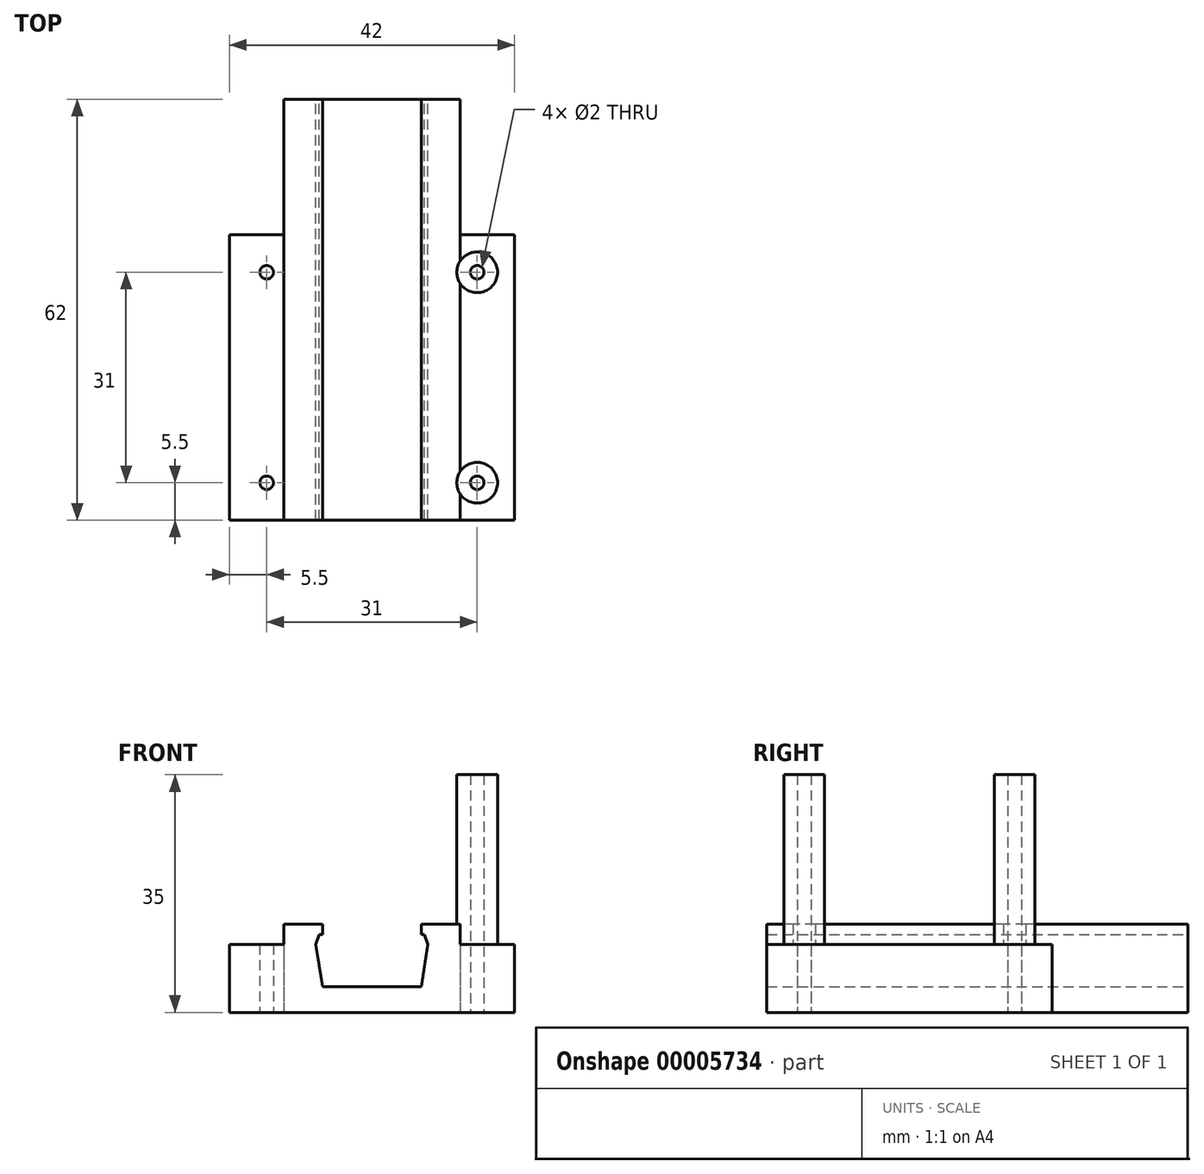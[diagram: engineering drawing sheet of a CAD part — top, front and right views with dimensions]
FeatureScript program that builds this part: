
annotation { "Feature Type Name" : "Feature", "Feature Type Description" : "" }
export const myFeature = defineFeature(function(context is Context, id is Id, definition is map)
    precondition{}
    {
        {
            var Q0;
            Q0=qCreatedBy(makeId("Top.planeOp"),FACE);
            var sketch = newSketch(context, id + "F0", { "sketchPlane" : qUnion([Q0])});
            skLineSegment(sketch, "E0.bottom", {"start": v(13, 0) * mm, "end": v(21, 0) * mm});
            skLineSegment(sketch, "E0.top", {"start": v(0, -42) * mm, "end": v(21, -42) * mm});
            skLineSegment(sketch, "E0.left", {"start": v(0, 0) * mm, "end": v(0, -42) * mm});
            skLineSegment(sketch, "E0.right", {"start": v(21, 0) * mm, "end": v(21, -42) * mm});
            skLineSegment(sketch, "E1.top", {"start": v(0, 20) * mm, "end": v(13, 20) * mm});
            skLineSegment(sketch, "E1.left", {"start": v(0, 0) * mm, "end": v(0, 20) * mm});
            skLineSegment(sketch, "E1.right", {"start": v(13, 0) * mm, "end": v(13, 20) * mm});
            skCircle(sketch, "E2", {"center": v(15.5, -5.5) * mm, "radius": 1 * mm});
            skCircle(sketch, "E3", {"center": v(15.5, -36.5) * mm, "radius": 1 * mm});
            skCircle(sketch, "E4.1.MirrorC", {"center": v(-15.5, -36.5) * mm, "radius": 1 * mm});
            skLineSegment(sketch, "E4.2.MirrorCS", {"start": v(-13, 0) * mm, "end": v(-13, 20) * mm});
            skCircle(sketch, "E4.3.MirrorC", {"center": v(-15.5, -5.5) * mm, "radius": 1 * mm});
            skLineSegment(sketch, "E4.4.MirrorCS", {"start": v(0, 20) * mm, "end": v(-13, 20) * mm});
            skLineSegment(sketch, "E4.6.MirrorCS", {"start": v(-13, 0) * mm, "end": v(-21, 0) * mm});
            skLineSegment(sketch, "E4.7.MirrorCS", {"start": v(0, -42) * mm, "end": v(-21, -42) * mm});
            skLineSegment(sketch, "E4.8.MirrorCS", {"start": v(-21, 0) * mm, "end": v(-21, -42) * mm});
            skSolve(sketch);
        }
        {
            var Q0;
            Q0=makeQuery(id+"F0.imprint","IMPRINT",FACE,{"disambiguationData":[TD([[makeQuery(id+"F0.imprint","IMPRINT",EDGE,{"derivedFrom":sQuery(id+"F0.wireOp",EDGE,"E1.left")}),1.0]])]});
            var Q1;
            Q1=makeQuery(id+"F0.imprint","IMPRINT",FACE,{"disambiguationData":[TD([[makeQuery(id+"F0.imprint","IMPRINT",EDGE,{"derivedFrom":sQuery(id+"F0.wireOp",EDGE,"E0.bottom")}),-1.0]])]});
            extrude(context, id + "F1", {"entities" : qUnion([Q0, Q1]), "depth" : 10 * mm});
        }
        {
            var Q0;
            Q0=makeQuery(id+"F1.opExtrude","CAP_FACE",FACE,{"disambiguationData":[OSD([sQuery(id+"F0.wireOp",EDGE,"E0.bottom"),sQuery(id+"F0.wireOp",EDGE,"E0.top"),sQuery(id+"F0.wireOp",EDGE,"E0.right"),sQuery(id+"F0.wireOp",EDGE,"E1.top"),sQuery(id+"F0.wireOp",EDGE,"E1.right"),sQuery(id+"F0.wireOp",EDGE,"E2"),sQuery(id+"F0.wireOp",EDGE,"E3"),sQuery(id+"F0.wireOp",EDGE,"E4.1.MirrorC"),sQuery(id+"F0.wireOp",EDGE,"E4.2.MirrorCS"),sQuery(id+"F0.wireOp",EDGE,"E4.3.MirrorC"),sQuery(id+"F0.wireOp",EDGE,"E4.4.MirrorCS"),sQuery(id+"F0.wireOp",EDGE,"E4.6.MirrorCS"),sQuery(id+"F0.wireOp",EDGE,"E4.7.MirrorCS"),sQuery(id+"F0.wireOp",EDGE,"E4.8.MirrorCS")])],"isStart":false});
            var sketch = newSketch(context, id + "F2", { "sketchPlane" : qUnion([Q0])});
            skLineSegment(sketch, "E5.bottom", {"start": v(-13, 20) * mm, "end": v(13, 20) * mm});
            skLineSegment(sketch, "E5.top", {"start": v(-13, -42) * mm, "end": v(13, -42) * mm});
            skLineSegment(sketch, "E5.left", {"start": v(-13, 20) * mm, "end": v(-13, -42) * mm});
            skLineSegment(sketch, "E5.right", {"start": v(13, 20) * mm, "end": v(13, -42) * mm});
            skLineSegment(sketch, "E6", {"start": v(0, 20) * mm, "end": v(0, 9.7) * mm});
            skLineSegment(sketch, "E7.bottom", {"start": v(-7.25, 20) * mm, "end": v(7.25, 20) * mm});
            skLineSegment(sketch, "E7.top", {"start": v(-7.25, -42) * mm, "end": v(7.25, -42) * mm});
            skLineSegment(sketch, "E7.left", {"start": v(-7.25, 20) * mm, "end": v(-7.25, -42) * mm});
            skLineSegment(sketch, "E7.right", {"start": v(7.25, 20) * mm, "end": v(7.25, -42) * mm});
            skSolve(sketch);
        }
        {
            var Q0;
            {var subQ0=sQuery(id+"F2.wireOp",EDGE,"E7.left");Q0=makeQuery(id+"F2.imprint","IMPRINT",FACE,{"disambiguationData":[TD([[makeQuery(id+"F2.imprint","IMPRINT",EDGE,{"derivedFrom":subQ0}),-1.0]])]});}
            var Q1;
            {var subQ0=sQuery(id+"F2.wireOp",EDGE,"E7.right");Q1=makeQuery(id+"F2.imprint","IMPRINT",FACE,{"disambiguationData":[TD([[makeQuery(id+"F2.imprint","IMPRINT",EDGE,{"derivedFrom":subQ0}),1.0]])]});}
            extrude(context, id + "F3", {"entities" : qUnion([Q0, Q1]), "operationType" : NewBodyOperationType.ADD, "depth" : 3 * mm});
        }
        {
            var Q0;
            {var subQ0=sQuery(id+"F2.wireOp",EDGE,"E5.bottom");Q0=makeQuery(id+"F3.boolean.opBoolean","MERGE",FACE,{"derivedFrom":[makeQuery(id+"F1.opExtrude","SWEPT_FACE",FACE,{"disambiguationData":[OSD([sQuery(id+"F0.wireOp",EDGE,"E1.top"),sQuery(id+"F0.wireOp",EDGE,"E4.4.MirrorCS")])]}),makeQuery(id+"F3.opExtrude","SWEPT_FACE",FACE,{"disambiguationData":[OSD([subQ0]),TDD([makeQuery(id+"F2.imprint","IMPRINT",EDGE,{"disambiguationData":[TD([[makeQuery(id+"F2.imprint","INTERSECT",VERTEX,{"derivedFrom":[subQ0,sQuery(id+"F2.wireOp",EDGE,"E5.right")]}),-1.0]])],"derivedFrom":subQ0})])]}),makeQuery(id+"F3.opExtrude","SWEPT_FACE",FACE,{"disambiguationData":[OSD([subQ0]),TDD([makeQuery(id+"F2.imprint","IMPRINT",EDGE,{"disambiguationData":[TD([[makeQuery(id+"F2.imprint","INTERSECT",VERTEX,{"derivedFrom":[subQ0,sQuery(id+"F2.wireOp",EDGE,"E5.left")]}),1.0]])],"derivedFrom":subQ0})])]})]});}
            var sketch = newSketch(context, id + "F4", { "sketchPlane" : qUnion([Q0])});
            skLineSegment(sketch, "E8", {"start": v(0, 0) * mm, "end": v(0, 11.5) * mm});
            skLineSegment(sketch, "E9", {"start": v(0, 3.8) * mm, "end": v(-7.25, 3.8) * mm});
            skLineSegment(sketch, "E10", {"start": v(-7.25, 3.8) * mm, "end": v(-8.25, 10) * mm});
            skLineSegment(sketch, "E11", {"start": v(-8.25, 10) * mm, "end": v(-7.75, 11.5) * mm});
            skLineSegment(sketch, "E12", {"start": v(-7.75, 11.5) * mm, "end": v(0, 11.5) * mm});
            skLineSegment(sketch, "E13.0.MirrorCS", {"start": v(0, 3.8) * mm, "end": v(7.25, 3.8) * mm});
            skLineSegment(sketch, "E14.0.MirrorCS", {"start": v(7.25, 3.8) * mm, "end": v(8.25, 10) * mm});
            skLineSegment(sketch, "E15.0.MirrorCS", {"start": v(8.25, 10) * mm, "end": v(7.75, 11.5) * mm});
            skLineSegment(sketch, "E16.0.MirrorCS", {"start": v(7.75, 11.5) * mm, "end": v(0, 11.5) * mm});
            skSolve(sketch);
        }
        {
            var Q0;
            {var subQ6=sQuery(id+"F4.wireOp",EDGE,"E13.0.MirrorCS");Q0=makeQuery(id+"F4.imprint","IMPRINT",FACE,{"disambiguationData":[TD([[makeQuery(id+"F4.imprint","IMPRINT",EDGE,{"derivedFrom":subQ6}),1.0]])]});}
            var Q1;
            {var subQ8=sQuery(id+"F4.wireOp",EDGE,"E9");Q1=makeQuery(id+"F4.imprint","IMPRINT",FACE,{"disambiguationData":[TD([[makeQuery(id+"F4.imprint","IMPRINT",EDGE,{"derivedFrom":subQ8}),-1.0]])]});}
            extrude(context, id + "F5", {"entities" : qUnion([Q0, Q1]), "operationType" : NewBodyOperationType.REMOVE, "endBound" : BoundingType.THROUGH_ALL, "oppositeDirection" : true, "depth" : 25 * mm});
        }
        {
            var Q0;
            {var subQ0=sQuery(id+"F0.wireOp",EDGE,"E0.bottom");var subQ1=sQuery(id+"F0.wireOp",EDGE,"E0.top");var subQ2=sQuery(id+"F0.wireOp",EDGE,"E0.right");var subQ3=sQuery(id+"F0.wireOp",EDGE,"E1.right");var subQ4=sQuery(id+"F0.wireOp",EDGE,"E2");var subQ5=sQuery(id+"F0.wireOp",EDGE,"E3");var subQ6=sQuery(id+"F0.wireOp",EDGE,"E4.7.MirrorCS");Q0=makeQuery(id+"F3.boolean.opBoolean","SPLIT",FACE,{"disambiguationData":[TD([makeQuery(id+"F1.opExtrude","SWEPT_FACE",FACE,{"disambiguationData":[OSD([subQ0])]})])],"derivedFrom":makeQuery(id+"F1.opExtrude","CAP_FACE",FACE,{"disambiguationData":[OSD([subQ0,subQ1,subQ2,sQuery(id+"F0.wireOp",EDGE,"E1.top"),subQ3,subQ4,subQ5,sQuery(id+"F0.wireOp",EDGE,"E4.1.MirrorC"),sQuery(id+"F0.wireOp",EDGE,"E4.2.MirrorCS"),sQuery(id+"F0.wireOp",EDGE,"E4.3.MirrorC"),sQuery(id+"F0.wireOp",EDGE,"E4.4.MirrorCS"),sQuery(id+"F0.wireOp",EDGE,"E4.6.MirrorCS"),subQ6,sQuery(id+"F0.wireOp",EDGE,"E4.8.MirrorCS")])],"isStart":false})});}
            var sketch = newSketch(context, id + "F6", { "sketchPlane" : qUnion([Q0])});
            skCircle(sketch, "E17.0", {"center": v(15.5, -5.5) * mm, "radius": 1 * mm});
            skCircle(sketch, "E18.0", {"center": v(15.5, -36.5) * mm, "radius": 1 * mm});
            skLineSegment(sketch, "E19", {"start": v(0, 0) * mm, "end": v(0, -29.55) * mm});
            skCircle(sketch, "E20", {"center": v(15.5, -5.5) * mm, "radius": 3 * mm});
            skCircle(sketch, "E21", {"center": v(15.5, -36.5) * mm, "radius": 3 * mm});
            skCircle(sketch, "E22.0.MirrorC", {"center": v(-15.5, -36.5) * mm, "radius": 3 * mm});
            skCircle(sketch, "E23.0.MirrorC", {"center": v(-15.5, -5.5) * mm, "radius": 3 * mm});
            skCircle(sketch, "E24.0.MirrorC", {"center": v(-15.5, -36.5) * mm, "radius": 1 * mm});
            skCircle(sketch, "E25.0.MirrorC", {"center": v(-15.5, -5.5) * mm, "radius": 1 * mm});
            skSolve(sketch);
        }
        {
            var Q0;
            {var subQ0=makeQuery(id+"F3.opExtrude","CAP_EDGE",EDGE,{"disambiguationData":[OSD([sQuery(id+"F2.wireOp",EDGE,"E5.right")])],"isStart":true});var subQ1=sQuery(id+"F6.wireOp",EDGE,"E20");var subQ3=makeQuery(id+"F6.imprint","INTERSECT",VERTEX,{"disambiguationData":[OD(0.0)],"derivedFrom":[subQ0,subQ1]});var subQ5=sQuery(id+"F6.wireOp",EDGE,"E21");var subQ7=makeQuery(id+"F6.imprint","INTERSECT",VERTEX,{"disambiguationData":[OD(0.0)],"derivedFrom":[subQ0,subQ5]});Q0=qUnion([makeQuery(id+"F6.imprint","IMPRINT",FACE,{"disambiguationData":[TD([[makeQuery(id+"F6.imprint","IMPRINT",EDGE,{"derivedFrom":sQuery(id+"F6.wireOp",EDGE,"E22.0.MirrorC")}),-1.0]])]}),makeQuery(id+"F6.imprint","IMPRINT",FACE,{"disambiguationData":[TD([[makeQuery(id+"F6.imprint","IMPRINT",EDGE,{"derivedFrom":sQuery(id+"F6.wireOp",EDGE,"E23.0.MirrorC")}),-1.0]])]}),makeQuery(id+"F6.imprint","IMPRINT",FACE,{"disambiguationData":[TD([[makeQuery(id+"F6.imprint","IMPRINT",EDGE,{"disambiguationData":[TD([[subQ3,-1.0]])],"derivedFrom":subQ1}),1.0]])]}),makeQuery(id+"F6.imprint","IMPRINT",FACE,{"disambiguationData":[TD([[makeQuery(id+"F6.imprint","IMPRINT",EDGE,{"disambiguationData":[TD([[subQ7,1.0]])],"derivedFrom":subQ5}),1.0]])]}),makeQuery(id+"F6.imprint","IMPRINT",FACE,{"disambiguationData":[TD([[makeQuery(id+"F6.imprint","IMPRINT",EDGE,{"derivedFrom":sQuery(id+"F6.wireOp",EDGE,"E17.0")}),-1.0]])]}),makeQuery(id+"F6.imprint","IMPRINT",FACE,{"disambiguationData":[TD([[makeQuery(id+"F6.imprint","IMPRINT",EDGE,{"derivedFrom":sQuery(id+"F6.wireOp",EDGE,"E18.0")}),-1.0]])]})]);}
            extrude(context, id + "F7", {"entities" : qUnion([Q0]), "operationType" : NewBodyOperationType.ADD, "depth" : 25 * mm});
        }
    });
